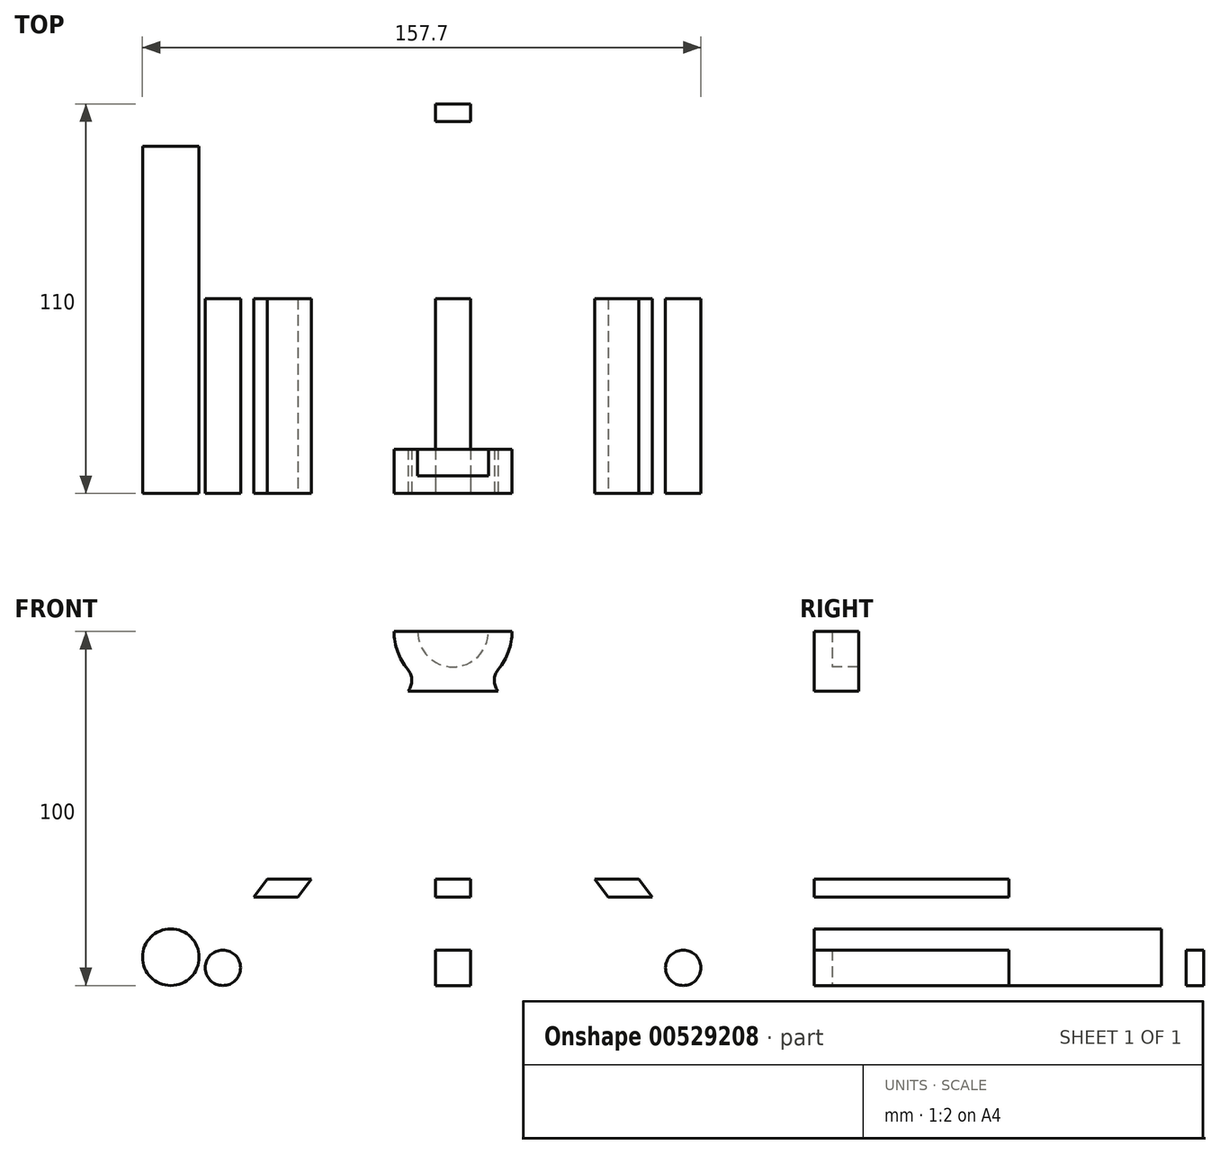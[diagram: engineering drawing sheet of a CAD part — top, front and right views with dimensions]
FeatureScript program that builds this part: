
annotation { "Feature Type Name" : "Feature", "Feature Type Description" : "" }
export const myFeature = defineFeature(function(context is Context, id is Id, definition is map)
    precondition{}
    {
        {
            var Q0;
            Q0=qCreatedBy(makeId("Front.planeOp"),FACE);
            var sketch = newSketch(context, id + "F0", { "sketchPlane" : qUnion([Q0])});
            skLineSegment(sketch, "E0", {"start": v(-65, 0) * mm, "end": v(0, 0) * mm});
            skLineSegment(sketch, "E1", {"start": v(-12.65, 83.13) * mm, "end": v(-69, 8) * mm});
            skLineSegment(sketch, "E2", {"start": v(-5, 15) * mm, "end": v(-5, 61.67) * mm});
            skLineSegment(sketch, "E3", {"start": v(-14, 64.67) * mm, "end": v(-49, 18) * mm});
            skLineSegment(sketch, "E4", {"start": v(-45, 10) * mm, "end": v(-10, 10) * mm});
            skArc(sketch, "E5", {"start": v(-16.67, 100) * mm, "mid": v(-15.67, 94.33) * mm, "end": v(-12.8, 89.33) * mm});
            skArc(sketch, "E6", {"start": v(-10, 100) * mm, "mid": v(-7.07, 92.93) * mm, "end": v(0, 90) * mm});
            skLineSegment(sketch, "E7", {"start": v(-10, 100) * mm, "end": v(-16.67, 100) * mm});
            skLineSegment(sketch, "E8", {"start": v(-10, 100) * mm, "end": v(0, 100) * mm});
            skLineSegment(sketch, "E9.MirrorCS", {"start": v(10, 100) * mm, "end": v(0, 100) * mm});
            skArc(sketch, "E10.MirrorCS", {"start": v(10, 100) * mm, "mid": v(7.07, 92.93) * mm, "end": v(0, 90) * mm});
            skLineSegment(sketch, "E11.MirrorCS", {"start": v(10, 100) * mm, "end": v(16.67, 100) * mm});
            skArc(sketch, "E12.MirrorCS", {"start": v(16.67, 100) * mm, "mid": v(15.67, 94.33) * mm, "end": v(12.8, 89.33) * mm});
            skLineSegment(sketch, "E13.MirrorCS", {"start": v(12.65, 83.13) * mm, "end": v(69, 8) * mm});
            skLineSegment(sketch, "E14.MirrorCS", {"start": v(14, 64.67) * mm, "end": v(49, 18) * mm});
            skLineSegment(sketch, "E15.MirrorCS", {"start": v(5, 15) * mm, "end": v(5, 61.67) * mm});
            skLineSegment(sketch, "E16.MirrorCS", {"start": v(45, 10) * mm, "end": v(10, 10) * mm});
            skLineSegment(sketch, "E17.MirrorCS", {"start": v(65, 0) * mm, "end": v(0, 0) * mm});
            skPoint(sketch, "E18.visualSharp", {"position": v(-75, 0) * mm});
            skArc(sketch, "E18.filletArc", {"start": v(-69, 8) * mm, "mid": v(-69.47, 2.76) * mm, "end": v(-65, 0) * mm});
            skPoint(sketch, "E19.visualSharp", {"position": v(-55, 10) * mm});
            skArc(sketch, "E19.filletArc", {"start": v(-49, 18) * mm, "mid": v(-49.47, 12.76) * mm, "end": v(-45, 10) * mm});
            skPoint(sketch, "E20.visualSharp", {"position": v(-5, 76.67) * mm});
            skArc(sketch, "E20.filletArc", {"start": v(-5, 61.67) * mm, "mid": v(-8.42, 66.41) * mm, "end": v(-14, 64.67) * mm});
            skPoint(sketch, "E21.visualSharp", {"position": v(-5, 10) * mm});
            skArc(sketch, "E21.filletArc", {"start": v(-10, 10) * mm, "mid": v(-6.46, 11.46) * mm, "end": v(-5, 15) * mm});
            skPoint(sketch, "E22.visualSharp", {"position": v(-10, 86.67) * mm});
            skArc(sketch, "E22.filletArc", {"start": v(-12.65, 83.13) * mm, "mid": v(-11.65, 86.26) * mm, "end": v(-12.8, 89.33) * mm});
            skPoint(sketch, "E23.visualSharp", {"position": v(5, 76.67) * mm});
            skArc(sketch, "E23.filletArc", {"start": v(14, 64.67) * mm, "mid": v(8.42, 66.41) * mm, "end": v(5, 61.67) * mm});
            skPoint(sketch, "E24.visualSharp", {"position": v(10, 86.67) * mm});
            skArc(sketch, "E24.filletArc", {"start": v(12.8, 89.33) * mm, "mid": v(11.65, 86.26) * mm, "end": v(12.65, 83.13) * mm});
            skPoint(sketch, "E25.visualSharp", {"position": v(5, 10) * mm});
            skArc(sketch, "E25.filletArc", {"start": v(5, 15) * mm, "mid": v(6.46, 11.46) * mm, "end": v(10, 10) * mm});
            skPoint(sketch, "E26.visualSharp", {"position": v(55, 10) * mm});
            skArc(sketch, "E26.filletArc", {"start": v(45, 10) * mm, "mid": v(49.47, 12.76) * mm, "end": v(49, 18) * mm});
            skPoint(sketch, "E27.visualSharp", {"position": v(75, 0) * mm});
            skArc(sketch, "E27.filletArc", {"start": v(65, 0) * mm, "mid": v(69.47, 2.76) * mm, "end": v(69, 8) * mm});
            skLineSegment(sketch, "E28.top", {"start": v(-5, 0) * mm, "end": v(0, 0) * mm});
            skLineSegment(sketch, "E28.left", {"start": v(-5, 10) * mm, "end": v(-5, 0) * mm});
            skLineSegment(sketch, "E29.MirrorCS", {"start": v(5, 10) * mm, "end": v(5, 0) * mm});
            skLineSegment(sketch, "E30", {"start": v(-5, 10) * mm, "end": v(5, 10) * mm});
            skLineSegment(sketch, "E31", {"start": v(-12.65, 83.13) * mm, "end": v(12.65, 83.13) * mm});
            skSolve(sketch);
        }
        {
            var Q0;
            Q0=makeQuery(id+"F0.imprint","IMPRINT",FACE,{"disambiguationData":[TD([[makeQuery(id+"F0.imprint","IMPRINT",EDGE,{"derivedFrom":sQuery(id+"F0.wireOp",EDGE,"E0")}),1.0]])]});
            var Q1;
            {var subQ1=sQuery(id+"F0.wireOp",EDGE,"E28.top");Q1=makeQuery(id+"F0.imprint","IMPRINT",FACE,{"disambiguationData":[TD([[makeQuery(id+"F0.imprint","IMPRINT",EDGE,{"derivedFrom":subQ1}),1.0]])]});}
            extrude(context, id + "F1", {"entities" : qUnion([Q0, Q1]), "oppositeDirection" : true, "depth" : 5 * mm, "offsetDistance" : 25 * mm});
        }
        {
            var Q0;
            Q0=makeQuery(id+"F0.imprint","IMPRINT",FACE,{"disambiguationData":[TD([[makeQuery(id+"F0.imprint","IMPRINT",EDGE,{"derivedFrom":sQuery(id+"F0.wireOp",EDGE,"E5")}),1.0]])]});
            extrude(context, id + "F2", {"entities" : qUnion([Q0]), "operationType" : NewBodyOperationType.ADD, "oppositeDirection" : true, "depth" : 12.5 * mm, "offsetDistance" : 25 * mm});
        }
        {
            var Q0;
            {var subQ0=sQuery(id+"F0.wireOp",EDGE,"E31");Q0=makeQuery(id+"F2.boolean.opBoolean","MERGE",FACE,{"derivedFrom":[makeQuery(id+"F1.opExtrude","CAP_FACE",FACE,{"disambiguationData":[OSD([sQuery(id+"F0.wireOp",EDGE,"E0"),sQuery(id+"F0.wireOp",EDGE,"E1"),sQuery(id+"F0.wireOp",EDGE,"E2"),sQuery(id+"F0.wireOp",EDGE,"E3"),sQuery(id+"F0.wireOp",EDGE,"E4"),sQuery(id+"F0.wireOp",EDGE,"E13.MirrorCS"),sQuery(id+"F0.wireOp",EDGE,"E14.MirrorCS"),sQuery(id+"F0.wireOp",EDGE,"E15.MirrorCS"),sQuery(id+"F0.wireOp",EDGE,"E16.MirrorCS"),sQuery(id+"F0.wireOp",EDGE,"E17.MirrorCS"),sQuery(id+"F0.wireOp",EDGE,"E18.filletArc"),sQuery(id+"F0.wireOp",EDGE,"E19.filletArc"),sQuery(id+"F0.wireOp",EDGE,"E20.filletArc"),sQuery(id+"F0.wireOp",EDGE,"E21.filletArc"),sQuery(id+"F0.wireOp",EDGE,"E23.filletArc"),sQuery(id+"F0.wireOp",EDGE,"E25.filletArc"),sQuery(id+"F0.wireOp",EDGE,"E26.filletArc"),sQuery(id+"F0.wireOp",EDGE,"E27.filletArc"),sQuery(id+"F0.wireOp",EDGE,"E28.top"),subQ0])],"isStart":true}),makeQuery(id+"F2.opExtrude","CAP_FACE",FACE,{"disambiguationData":[OSD([sQuery(id+"F0.wireOp",EDGE,"E5"),sQuery(id+"F0.wireOp",EDGE,"E6"),sQuery(id+"F0.wireOp",EDGE,"E7"),sQuery(id+"F0.wireOp",EDGE,"E10.MirrorCS"),sQuery(id+"F0.wireOp",EDGE,"E11.MirrorCS"),sQuery(id+"F0.wireOp",EDGE,"E12.MirrorCS"),sQuery(id+"F0.wireOp",EDGE,"E22.filletArc"),sQuery(id+"F0.wireOp",EDGE,"E24.filletArc"),subQ0])],"isStart":true})]});}
            var sketch = newSketch(context, id + "F3", { "sketchPlane" : qUnion([Q0])});
            skLineSegment(sketch, "E32", {"start": v(-10, 100) * mm, "end": v(10, 100) * mm});
            skArc(sketch, "E33", {"start": v(-10, 100) * mm, "mid": v(0, 90) * mm, "end": v(10, 100) * mm});
            skPoint(sketch, "E34.end.orphan", {"position": v(0, 90) * mm});
            skSolve(sketch);
        }
        {
            var Q0;
            Q0 = qSketchRegion(id + "F3", true);
            extrude(context, id + "F4", {"entities" : qUnion([Q0]), "operationType" : NewBodyOperationType.ADD, "oppositeDirection" : true, "depth" : 5 * mm, "offsetDistance" : 25 * mm});
        }
        {
            var Q0;
            {var subQ0=sQuery(id+"F0.wireOp",EDGE,"E31");Q0=makeQuery(id+"F4.boolean.opBoolean","MERGE",FACE,{"derivedFrom":[makeQuery(id+"F2.boolean.opBoolean","MERGE",FACE,{"derivedFrom":[makeQuery(id+"F1.opExtrude","CAP_FACE",FACE,{"disambiguationData":[OSD([sQuery(id+"F0.wireOp",EDGE,"E0"),sQuery(id+"F0.wireOp",EDGE,"E1"),sQuery(id+"F0.wireOp",EDGE,"E2"),sQuery(id+"F0.wireOp",EDGE,"E3"),sQuery(id+"F0.wireOp",EDGE,"E4"),sQuery(id+"F0.wireOp",EDGE,"E13.MirrorCS"),sQuery(id+"F0.wireOp",EDGE,"E14.MirrorCS"),sQuery(id+"F0.wireOp",EDGE,"E15.MirrorCS"),sQuery(id+"F0.wireOp",EDGE,"E16.MirrorCS"),sQuery(id+"F0.wireOp",EDGE,"E17.MirrorCS"),sQuery(id+"F0.wireOp",EDGE,"E18.filletArc"),sQuery(id+"F0.wireOp",EDGE,"E19.filletArc"),sQuery(id+"F0.wireOp",EDGE,"E20.filletArc"),sQuery(id+"F0.wireOp",EDGE,"E21.filletArc"),sQuery(id+"F0.wireOp",EDGE,"E23.filletArc"),sQuery(id+"F0.wireOp",EDGE,"E25.filletArc"),sQuery(id+"F0.wireOp",EDGE,"E26.filletArc"),sQuery(id+"F0.wireOp",EDGE,"E27.filletArc"),sQuery(id+"F0.wireOp",EDGE,"E28.top"),subQ0])],"isStart":true}),makeQuery(id+"F2.opExtrude","CAP_FACE",FACE,{"disambiguationData":[OSD([sQuery(id+"F0.wireOp",EDGE,"E5"),sQuery(id+"F0.wireOp",EDGE,"E6"),sQuery(id+"F0.wireOp",EDGE,"E7"),sQuery(id+"F0.wireOp",EDGE,"E10.MirrorCS"),sQuery(id+"F0.wireOp",EDGE,"E11.MirrorCS"),sQuery(id+"F0.wireOp",EDGE,"E12.MirrorCS"),sQuery(id+"F0.wireOp",EDGE,"E22.filletArc"),sQuery(id+"F0.wireOp",EDGE,"E24.filletArc"),subQ0])],"isStart":true})]}),makeQuery(id+"F4.opExtrude","CAP_FACE",FACE,{"disambiguationData":[OSD([sQuery(id+"F3.wireOp",EDGE,"E32"),sQuery(id+"F3.wireOp",EDGE,"E33")])],"isStart":true})]});}
            var sketch = newSketch(context, id + "F5", { "sketchPlane" : qUnion([Q0])});
            skLineSegment(sketch, "E35.bottom", {"start": v(-5, 30) * mm, "end": v(5, 30) * mm});
            skLineSegment(sketch, "E35.top", {"start": v(-5, 25) * mm, "end": v(5, 25) * mm});
            skLineSegment(sketch, "E35.left", {"start": v(-5, 30) * mm, "end": v(-5, 25) * mm});
            skLineSegment(sketch, "E35.right", {"start": v(5, 30) * mm, "end": v(5, 25) * mm});
            skLineSegment(sketch, "E36", {"start": v(-43.75, 25) * mm, "end": v(-56.25, 25) * mm});
            skLineSegment(sketch, "E37", {"start": v(-40, 30) * mm, "end": v(-52.5, 30) * mm});
            skLineSegment(sketch, "E38", {"start": v(-43.75, 25) * mm, "end": v(-40, 30) * mm});
            skLineSegment(sketch, "E39", {"start": v(-52.5, 30) * mm, "end": v(-56.25, 25) * mm});
            skLineSegment(sketch, "E40.MirrorCS", {"start": v(43.75, 25) * mm, "end": v(40, 30) * mm});
            skLineSegment(sketch, "E41.MirrorCS", {"start": v(40, 30) * mm, "end": v(52.5, 30) * mm});
            skLineSegment(sketch, "E42.MirrorCS", {"start": v(52.5, 30) * mm, "end": v(56.25, 25) * mm});
            skLineSegment(sketch, "E43.MirrorCS", {"start": v(43.75, 25) * mm, "end": v(56.25, 25) * mm});
            skPoint(sketch, "E44.right.end.orphan", {"position": v(-55, 5) * mm});
            skPoint(sketch, "E44.bottom.end.orphan", {"position": v(-55, 0) * mm});
            skPoint(sketch, "E44.left.end.orphan", {"position": v(-65, 5) * mm});
            skPoint(sketch, "E44.left.start.orphan", {"position": v(-65, 0) * mm});
            skPoint(sketch, "E45.MirrorCS.end.orphan", {"position": v(55, 5) * mm});
            skPoint(sketch, "E45.MirrorCS.start.orphan", {"position": v(55, 0) * mm});
            skPoint(sketch, "E46.MirrorCS.start.orphan", {"position": v(65, 5) * mm});
            skPoint(sketch, "E47.MirrorCS.start.orphan", {"position": v(65, 0) * mm});
            skCircle(sketch, "E48", {"center": v(-65, 5) * mm, "radius": 5 * mm});
            skCircle(sketch, "E49.MirrorC", {"center": v(65, 5) * mm, "radius": 5 * mm});
            skSolve(sketch);
        }
        {
            var Q0;
            Q0 = qSketchRegion(id + "F5", true);
            extrude(context, id + "F6", {"entities" : qUnion([Q0]), "operationType" : NewBodyOperationType.ADD, "oppositeDirection" : true, "depth" : 55 * mm, "offsetDistance" : 25 * mm});
        }
        {
            var Q0;
            Q0=makeQuery(id+"F1.opExtrude","SWEPT_BODY",BODY,{"disambiguationData":[OSD([sQuery(id+"F0.wireOp",EDGE,"E0"),sQuery(id+"F0.wireOp",EDGE,"E1"),sQuery(id+"F0.wireOp",EDGE,"E2"),sQuery(id+"F0.wireOp",EDGE,"E3"),sQuery(id+"F0.wireOp",EDGE,"E4"),sQuery(id+"F0.wireOp",EDGE,"E13.MirrorCS"),sQuery(id+"F0.wireOp",EDGE,"E14.MirrorCS"),sQuery(id+"F0.wireOp",EDGE,"E15.MirrorCS"),sQuery(id+"F0.wireOp",EDGE,"E16.MirrorCS"),sQuery(id+"F0.wireOp",EDGE,"E17.MirrorCS"),sQuery(id+"F0.wireOp",EDGE,"E18.filletArc"),sQuery(id+"F0.wireOp",EDGE,"E19.filletArc"),sQuery(id+"F0.wireOp",EDGE,"E20.filletArc"),sQuery(id+"F0.wireOp",EDGE,"E21.filletArc"),sQuery(id+"F0.wireOp",EDGE,"E23.filletArc"),sQuery(id+"F0.wireOp",EDGE,"E25.filletArc"),sQuery(id+"F0.wireOp",EDGE,"E26.filletArc"),sQuery(id+"F0.wireOp",EDGE,"E27.filletArc"),sQuery(id+"F0.wireOp",EDGE,"E28.top"),sQuery(id+"F0.wireOp",EDGE,"E31")])]});
            var Q1;
            Q1=makeQuery(id+"F6.opExtrude","CAP_FACE",FACE,{"disambiguationData":[OSD([sQuery(id+"F5.wireOp",EDGE,"E49.MirrorC")])],"isStart":false});
            mirror(context, id + "F7", {"operationType" : NewBodyOperationType.ADD, "entities" : qUnion([Q0]), "mirrorPlane" : qUnion([Q1])});
        }
        {
            var Q0;
            Q0=qCreatedBy(makeId("Front.planeOp"),FACE);
            var sketch = newSketch(context, id + "F8", { "sketchPlane" : qUnion([Q0])});
            skCircle(sketch, "E50", {"center": v(-79.7, 8) * mm, "radius": 8 * mm});
            skPoint(sketch, "E51.start.orphan", {"position": v(-80.2, 0) * mm});
            skSolve(sketch);
        }
        {
            var Q0;
            Q0 = qSketchRegion(id + "F8", true);
            extrude(context, id + "F9", {"entities" : qUnion([Q0]), "oppositeDirection" : true, "depth" : 98 * mm, "offsetDistance" : 25 * mm});
        }
    });
